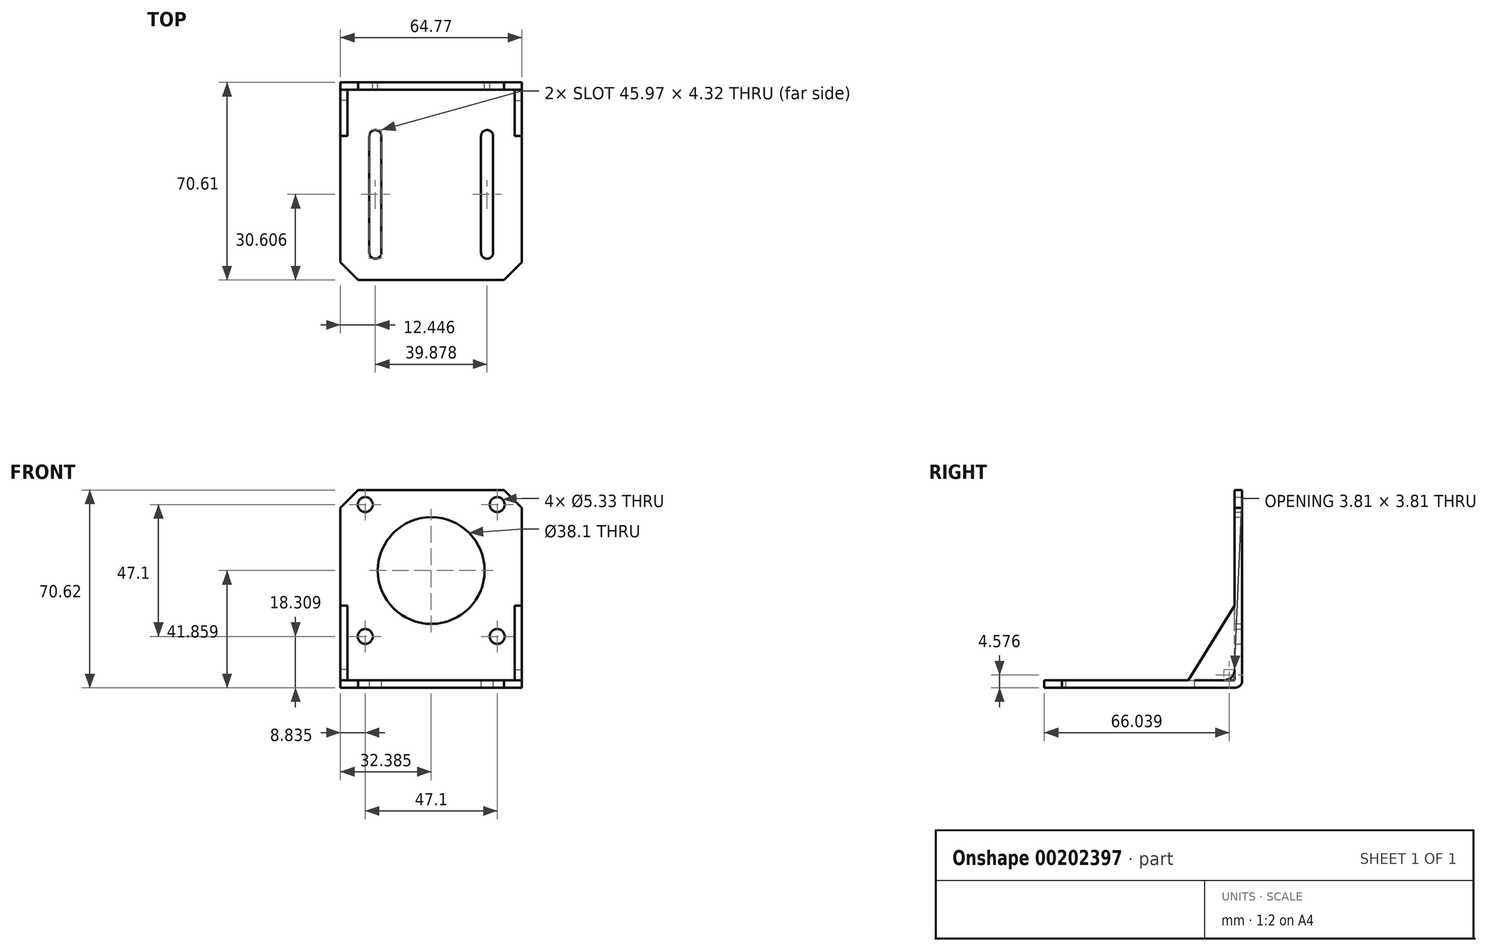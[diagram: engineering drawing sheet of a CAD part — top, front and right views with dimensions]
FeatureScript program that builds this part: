
annotation { "Feature Type Name" : "Feature", "Feature Type Description" : "" }
export const myFeature = defineFeature(function(context is Context, id is Id, definition is map)
    precondition{}
    {
        {
            var Q0;
            Q0=qCreatedBy(makeId("Right.planeOp"),FACE);
            var sketch = newSketch(context, id + "F0", { "sketchPlane" : qUnion([Q0])});
            skLineSegment(sketch, "E0", {"start": v(-61.38, 56.25) * mm, "end": v(-58.7, 56.25) * mm});
            skLineSegment(sketch, "E1", {"start": v(-58.7, 56.25) * mm, "end": v(-58.7, -11.83) * mm});
            skLineSegment(sketch, "E2", {"start": v(-61.25, -14.37) * mm, "end": v(-129.32, -14.37) * mm});
            skLineSegment(sketch, "E3", {"start": v(-129.32, -14.37) * mm, "end": v(-129.32, -11.7) * mm});
            skLineSegment(sketch, "E4", {"start": v(-129.32, -11.7) * mm, "end": v(-61.38, -11.7) * mm});
            skLineSegment(sketch, "E5", {"start": v(-61.38, -11.7) * mm, "end": v(-61.38, 56.25) * mm});
            skPoint(sketch, "E6.visualSharp", {"position": v(-58.7, -14.37) * mm});
            skArc(sketch, "E6.filletArc", {"start": v(-61.25, -14.37) * mm, "mid": v(-59.45, -13.62) * mm, "end": v(-58.7, -11.83) * mm});
            skSolve(sketch);
        }
        {
            var Q0;
            Q0=makeQuery(id+"F0.imprint","IMPRINT",FACE,{"disambiguationData":[TD([[makeQuery(id+"F0.imprint","IMPRINT",EDGE,{"derivedFrom":sQuery(id+"F0.wireOp",EDGE,"E0")}),-1.0]])]});
            extrude(context, id + "F1", {"entities" : qUnion([Q0]), "depth" : 64.77 * mm});
        }
        {
            var Q0;
            Q0=makeQuery(id+"F1.opExtrude","CAP_FACE",FACE,{"disambiguationData":[OSD([sQuery(id+"F0.wireOp",EDGE,"E0"),sQuery(id+"F0.wireOp",EDGE,"E1"),sQuery(id+"F0.wireOp",EDGE,"E2"),sQuery(id+"F0.wireOp",EDGE,"E3"),sQuery(id+"F0.wireOp",EDGE,"E4"),sQuery(id+"F0.wireOp",EDGE,"E5"),sQuery(id+"F0.wireOp",EDGE,"E6.filletArc")])],"isStart":false});
            var sketch = newSketch(context, id + "F2", { "sketchPlane" : qUnion([Q0])});
            skLineSegment(sketch, "E7", {"start": v(-61.38, 14.97) * mm, "end": v(-77.89, -11.7) * mm});
            skLineSegment(sketch, "E8", {"start": v(-77.89, -11.7) * mm, "end": v(-65.19, -11.7) * mm});
            skLineSegment(sketch, "E9", {"start": v(-61.38, -7.89) * mm, "end": v(-61.38, 14.97) * mm});
            skPoint(sketch, "E10.visualSharp", {"position": v(-61.38, -11.7) * mm});
            skArc(sketch, "E10.filletArc", {"start": v(-65.19, -11.7) * mm, "mid": v(-62.5, -10.58) * mm, "end": v(-61.38, -7.89) * mm});
            skSolve(sketch);
        }
        {
            var Q0;
            Q0=makeQuery(id+"F1.opExtrude","CAP_FACE",FACE,{"disambiguationData":[OSD([sQuery(id+"F0.wireOp",EDGE,"E0"),sQuery(id+"F0.wireOp",EDGE,"E1"),sQuery(id+"F0.wireOp",EDGE,"E2"),sQuery(id+"F0.wireOp",EDGE,"E3"),sQuery(id+"F0.wireOp",EDGE,"E4"),sQuery(id+"F0.wireOp",EDGE,"E5"),sQuery(id+"F0.wireOp",EDGE,"E6.filletArc")])],"isStart":true});
            var sketch = newSketch(context, id + "F3", { "sketchPlane" : qUnion([Q0])});
            skLineSegment(sketch, "E11", {"start": v(61.38, 14.97) * mm, "end": v(77.89, -11.7) * mm});
            skLineSegment(sketch, "E12", {"start": v(77.89, -11.7) * mm, "end": v(65.19, -11.7) * mm});
            skLineSegment(sketch, "E13", {"start": v(61.38, -7.89) * mm, "end": v(61.38, 14.97) * mm});
            skPoint(sketch, "E14.visualSharp", {"position": v(61.38, -11.7) * mm});
            skArc(sketch, "E14.filletArc", {"start": v(61.38, -7.89) * mm, "mid": v(62.5, -10.58) * mm, "end": v(65.19, -11.7) * mm});
            skSolve(sketch);
        }
        {
            var Q0;
            Q0=makeQuery(id+"F3.imprint","IMPRINT",FACE,{"disambiguationData":[TD([[makeQuery(id+"F3.imprint","IMPRINT",EDGE,{"derivedFrom":sQuery(id+"F3.wireOp",EDGE,"E11")}),-1.0]])]});
            extrude(context, id + "F4", {"entities" : qUnion([Q0]), "operationType" : NewBodyOperationType.ADD, "oppositeDirection" : true, "depth" : 2.54 * mm});
        }
        {
            var Q0;
            Q0=makeQuery(id+"F2.imprint","IMPRINT",FACE,{"disambiguationData":[TD([[makeQuery(id+"F2.imprint","IMPRINT",EDGE,{"derivedFrom":sQuery(id+"F2.wireOp",EDGE,"E7")}),1.0]])]});
            extrude(context, id + "F5", {"entities" : qUnion([Q0]), "operationType" : NewBodyOperationType.ADD, "oppositeDirection" : true, "depth" : 2.54 * mm});
        }
        {
            var Q0;
            Q0=makeQuery(id+"F1.opExtrude","SWEPT_FACE",FACE,{"disambiguationData":[OSD([sQuery(id+"F0.wireOp",EDGE,"E1")])]});
            var sketch = newSketch(context, id + "F6", { "sketchPlane" : qUnion([Q0])});
            skLineSegment(sketch, "E15", {"start": v(-64.77, 49.9) * mm, "end": v(-58.42, 56.25) * mm});
            skLineSegment(sketch, "E16", {"start": v(-6.35, 56.25) * mm, "end": v(0, 49.9) * mm});
            skCircle(sketch, "E17", {"center": v(-55.94, 51.04) * mm, "radius": 2.67 * mm});
            skCircle(sketch, "E18", {"center": v(-8.84, 51.04) * mm, "radius": 2.67 * mm});
            skCircle(sketch, "E19", {"center": v(-55.94, 3.94) * mm, "radius": 2.67 * mm});
            skCircle(sketch, "E20", {"center": v(-8.84, 3.94) * mm, "radius": 2.67 * mm});
            skCircle(sketch, "E21", {"center": v(-32.39, 27.49) * mm, "radius": 19.05 * mm});
            skPoint(sketch, "E22", {"position": v(-32.39, 56.25) * mm});
            skLineSegment(sketch, "E23", {"start": v(-55.94, 51.04) * mm, "end": v(-64.77, 51.04) * mm, "construction": true});
            skLineSegment(sketch, "E24", {"start": v(-8.84, 51.04) * mm, "end": v(0, 51.04) * mm, "construction": true});
            skLineSegment(sketch, "E25", {"start": v(-55.94, 51.04) * mm, "end": v(-55.94, 3.94) * mm, "construction": true});
            skPoint(sketch, "E26", {"position": v(-55.94, 27.49) * mm});
            skSolve(sketch);
        }
        {
            var Q0;
            {var subQ2=sQuery(id+"F6.wireOp",EDGE,"E15");Q0=makeQuery(id+"F6.imprint","IMPRINT",FACE,{"disambiguationData":[TD([[makeQuery(id+"F6.imprint","IMPRINT",EDGE,{"derivedFrom":subQ2}),1.0]])]});}
            var Q1;
            Q1=makeQuery(id+"F6.imprint","IMPRINT",FACE,{"disambiguationData":[TD([[makeQuery(id+"F6.imprint","IMPRINT",EDGE,{"derivedFrom":sQuery(id+"F6.wireOp",EDGE,"E17")}),1.0]])]});
            var Q2;
            Q2=makeQuery(id+"F6.imprint","IMPRINT",FACE,{"disambiguationData":[TD([[makeQuery(id+"F6.imprint","IMPRINT",EDGE,{"derivedFrom":sQuery(id+"F6.wireOp",EDGE,"E18")}),1.0]])]});
            var Q3;
            {var subQ2=sQuery(id+"F6.wireOp",EDGE,"E16");Q3=makeQuery(id+"F6.imprint","IMPRINT",FACE,{"disambiguationData":[TD([[makeQuery(id+"F6.imprint","IMPRINT",EDGE,{"derivedFrom":subQ2}),1.0]])]});}
            var Q4;
            Q4=makeQuery(id+"F6.imprint","IMPRINT",FACE,{"disambiguationData":[TD([[makeQuery(id+"F6.imprint","IMPRINT",EDGE,{"derivedFrom":sQuery(id+"F6.wireOp",EDGE,"E21")}),1.0]])]});
            var Q5;
            Q5=makeQuery(id+"F6.imprint","IMPRINT",FACE,{"disambiguationData":[TD([[makeQuery(id+"F6.imprint","IMPRINT",EDGE,{"derivedFrom":sQuery(id+"F6.wireOp",EDGE,"E19")}),1.0]])]});
            var Q6;
            Q6=makeQuery(id+"F6.imprint","IMPRINT",FACE,{"disambiguationData":[TD([[makeQuery(id+"F6.imprint","IMPRINT",EDGE,{"derivedFrom":sQuery(id+"F6.wireOp",EDGE,"E20")}),1.0]])]});
            extrude(context, id + "F7", {"entities" : qUnion([Q0, Q1, Q2, Q3, Q4, Q5, Q6]), "operationType" : NewBodyOperationType.REMOVE, "endBound" : BoundingType.THROUGH_ALL, "oppositeDirection" : true, "depth" : 25.4 * mm});
        }
        {
            var Q0;
            Q0=makeQuery(id+"F1.opExtrude","SWEPT_FACE",FACE,{"disambiguationData":[OSD([sQuery(id+"F0.wireOp",EDGE,"E2")])]});
            var sketch = newSketch(context, id + "F8", { "sketchPlane" : qUnion([Q0])});
            skLineSegment(sketch, "E27", {"start": v(0, 122.97) * mm, "end": v(6.35, 129.32) * mm});
            skLineSegment(sketch, "E28", {"start": v(58.42, 129.32) * mm, "end": v(64.77, 122.97) * mm});
            skArc(sketch, "E29", {"start": v(14.6, 119.54) * mm, "mid": v(12.45, 121.7) * mm, "end": v(10.29, 119.54) * mm});
            skArc(sketch, "E30", {"start": v(10.29, 77.89) * mm, "mid": v(12.45, 75.73) * mm, "end": v(14.6, 77.89) * mm});
            skLineSegment(sketch, "E31", {"start": v(10.29, 119.54) * mm, "end": v(10.29, 77.89) * mm});
            skLineSegment(sketch, "E32", {"start": v(14.6, 119.54) * mm, "end": v(14.6, 77.89) * mm});
            skArc(sketch, "E33", {"start": v(54.48, 119.54) * mm, "mid": v(52.32, 121.7) * mm, "end": v(50.17, 119.54) * mm});
            skArc(sketch, "E34", {"start": v(50.17, 77.89) * mm, "mid": v(52.32, 75.73) * mm, "end": v(54.48, 77.89) * mm});
            skLineSegment(sketch, "E35", {"start": v(50.17, 77.89) * mm, "end": v(50.17, 119.54) * mm});
            skLineSegment(sketch, "E36", {"start": v(54.48, 77.89) * mm, "end": v(54.48, 119.54) * mm});
            skLineSegment(sketch, "E37", {"start": v(12.45, 119.54) * mm, "end": v(0, 119.54) * mm, "construction": true});
            skLineSegment(sketch, "E38", {"start": v(52.32, 119.54) * mm, "end": v(64.77, 119.54) * mm, "construction": true});
            skSolve(sketch);
        }
        {
            var Q0;
            {var subQ2=sQuery(id+"F8.wireOp",EDGE,"E27");Q0=makeQuery(id+"F8.imprint","IMPRINT",FACE,{"disambiguationData":[TD([[makeQuery(id+"F8.imprint","IMPRINT",EDGE,{"derivedFrom":subQ2}),1.0]])]});}
            var Q1;
            Q1=makeQuery(id+"F8.imprint","IMPRINT",FACE,{"disambiguationData":[TD([[makeQuery(id+"F8.imprint","IMPRINT",EDGE,{"derivedFrom":sQuery(id+"F8.wireOp",EDGE,"E29")}),1.0]])]});
            var Q2;
            Q2=makeQuery(id+"F8.imprint","IMPRINT",FACE,{"disambiguationData":[TD([[makeQuery(id+"F8.imprint","IMPRINT",EDGE,{"derivedFrom":sQuery(id+"F8.wireOp",EDGE,"E33")}),1.0]])]});
            var Q3;
            {var subQ2=sQuery(id+"F8.wireOp",EDGE,"E28");Q3=makeQuery(id+"F8.imprint","IMPRINT",FACE,{"disambiguationData":[TD([[makeQuery(id+"F8.imprint","IMPRINT",EDGE,{"derivedFrom":subQ2}),1.0]])]});}
            extrude(context, id + "F9", {"entities" : qUnion([Q0, Q1, Q2, Q3]), "operationType" : NewBodyOperationType.REMOVE, "endBound" : BoundingType.THROUGH_ALL, "oppositeDirection" : true, "depth" : 25.4 * mm});
        }
    });
